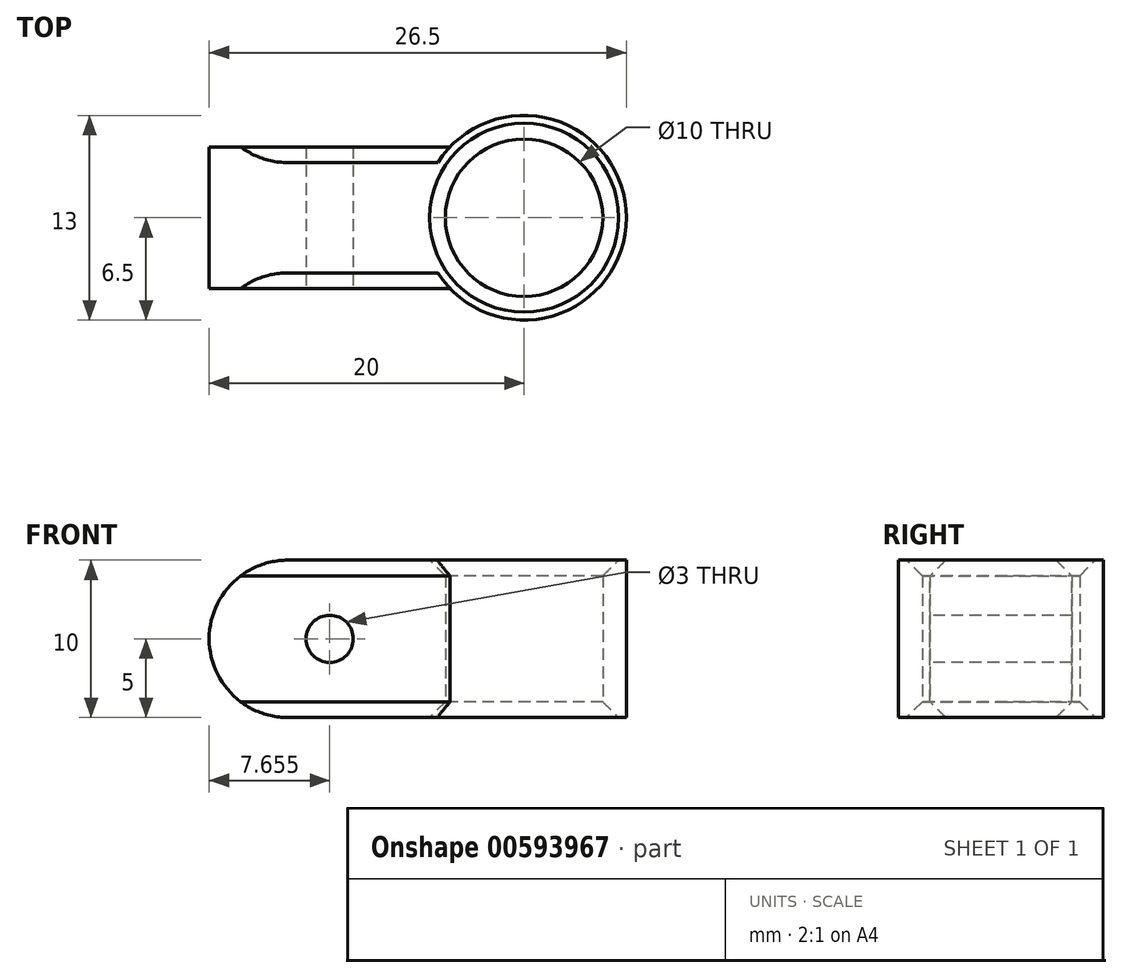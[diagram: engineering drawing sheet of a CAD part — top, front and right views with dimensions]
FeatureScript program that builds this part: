
annotation { "Feature Type Name" : "Feature", "Feature Type Description" : "" }
export const myFeature = defineFeature(function(context is Context, id is Id, definition is map)
    precondition{}
    {
        {
            var Q0;
            Q0=qCreatedBy(makeId("Top.planeOp"),FACE);
            var sketch = newSketch(context, id + "F0", { "sketchPlane" : qUnion([Q0])});
            skLineSegment(sketch, "E0.bottom", {"start": v(-10, 4.5) * mm, "end": v(10, 4.5) * mm});
            skLineSegment(sketch, "E0.top", {"start": v(-10, -4.5) * mm, "end": v(10, -4.5) * mm});
            skLineSegment(sketch, "E0.left", {"start": v(-10, 4.5) * mm, "end": v(-10, -4.5) * mm});
            skLineSegment(sketch, "E0.right", {"start": v(10, 4.5) * mm, "end": v(10, -4.5) * mm});
            skPoint(sketch, "E0.middle", {"position": v(0, 0) * mm});
            skCircle(sketch, "E1", {"center": v(10, 0) * mm, "radius": 5 * mm});
            skCircle(sketch, "E2", {"center": v(10, 0) * mm, "radius": 6.5 * mm});
            skSolve(sketch);
        }
        {
            var Q0;
            {var subQ0=sQuery(id+"F0.wireOp",EDGE,"E0.left");Q0=makeQuery(id+"F0.imprint","IMPRINT",FACE,{"disambiguationData":[TD([[makeQuery(id+"F0.imprint","IMPRINT",EDGE,{"derivedFrom":subQ0}),1.0]])]});}
            var Q1;
            {var subQ0=sQuery(id+"F0.wireOp",EDGE,"E2");var subQ1=sQuery(id+"F0.wireOp",EDGE,"E0.bottom");var subQ2=makeQuery(id+"F0.imprint","INTERSECT",VERTEX,{"derivedFrom":[subQ1,subQ0]});Q1=makeQuery(id+"F0.imprint","IMPRINT",FACE,{"disambiguationData":[TD([[makeQuery(id+"F0.imprint","IMPRINT",EDGE,{"disambiguationData":[TD([[subQ2,-1.0]])],"derivedFrom":subQ1}),-1.0]])]});}
            var Q2;
            {var subQ0=sQuery(id+"F0.wireOp",EDGE,"E2");var subQ1=sQuery(id+"F0.wireOp",EDGE,"E0.bottom");var subQ2=makeQuery(id+"F0.imprint","INTERSECT",VERTEX,{"derivedFrom":[subQ1,subQ0]});Q2=makeQuery(id+"F0.imprint","IMPRINT",FACE,{"disambiguationData":[TD([[makeQuery(id+"F0.imprint","IMPRINT",EDGE,{"disambiguationData":[TD([[subQ2,-1.0]])],"derivedFrom":subQ1}),1.0]])]});}
            extrude(context, id + "F1", {"entities" : qUnion([Q0, Q1, Q2]), "depth" : 10 * mm, "offsetDistance" : 25 * mm});
        }
        {
            var Q0;
            Q0=makeQuery(id+"F1.opExtrude","SWEPT_FACE",FACE,{"disambiguationData":[OSD([sQuery(id+"F0.wireOp",EDGE,"E0.top")])]});
            var sketch = newSketch(context, id + "F2", { "sketchPlane" : qUnion([Q0])});
            skLineSegment(sketch, "E3", {"start": v(-10, 10) * mm, "end": v(5.3, 0) * mm});
            skLineSegment(sketch, "E4", {"start": v(5.3, 10) * mm, "end": v(-10, 0) * mm});
            skPoint(sketch, "E5", {"position": v(-2.35, 5) * mm});
            skSolve(sketch);
        }
        {
            var Q0;
            Q0=sQuery(id+"F2.wireOp",VERTEX,"E5");
            var Q1;
            Q1=makeQuery(id+"F1.opExtrude","SWEPT_BODY",BODY,{"disambiguationData":[OSD([sQuery(id+"F0.wireOp",EDGE,"E0.bottom"),sQuery(id+"F0.wireOp",EDGE,"E0.top"),sQuery(id+"F0.wireOp",EDGE,"E0.left"),sQuery(id+"F0.wireOp",EDGE,"E1"),sQuery(id+"F0.wireOp",EDGE,"E2")])]});
            hole(context, id + "F3", {"style" : HoleStyle.SIMPLE, "endStyle" : HoleEndStyle.BLIND, "holeDiameter" : 3 * mm, "majorDiameter" : 5 * mm, "holeDepth" : 30 * mm, "isTappedThrough" : true, "tappedDepth" : 12 * mm, "tapClearance" : 3, "locations" : qUnion([Q0]), "scope" : qUnion([Q1])});
        }
        {
            var Q0;
            Q0=makeQuery(id+"F1.opExtrude","CAP_EDGE",EDGE,{"disambiguationData":[OSD([sQuery(id+"F0.wireOp",EDGE,"E1")])],"isStart":false});
            var Q1;
            Q1=makeQuery(id+"F1.opExtrude","CAP_EDGE",EDGE,{"disambiguationData":[OSD([sQuery(id+"F0.wireOp",EDGE,"E1")])],"isStart":true});
            var Q2;
            Q2=makeQuery(id+"F1.opExtrude","CAP_EDGE",EDGE,{"disambiguationData":[OSD([sQuery(id+"F0.wireOp",EDGE,"E0.bottom")])],"isStart":false});
            var Q3;
            Q3=makeQuery(id+"F1.opExtrude","CAP_EDGE",EDGE,{"disambiguationData":[OSD([sQuery(id+"F0.wireOp",EDGE,"E0.top")])],"isStart":false});
            var Q4;
            Q4=makeQuery(id+"F1.opExtrude","CAP_EDGE",EDGE,{"disambiguationData":[OSD([sQuery(id+"F0.wireOp",EDGE,"E0.top")])],"isStart":true});
            var Q5;
            Q5=makeQuery(id+"F1.opExtrude","CAP_EDGE",EDGE,{"disambiguationData":[OSD([sQuery(id+"F0.wireOp",EDGE,"E0.bottom")])],"isStart":true});
            chamfer(context, id + "F4", {"entities" : qUnion([Q0, Q1, Q2, Q3, Q4, Q5]), "width" : 1 * mm});
        }
        {
            var Q0;
            Q0=makeQuery(id+"F1.opExtrude","CAP_EDGE",EDGE,{"disambiguationData":[OSD([sQuery(id+"F0.wireOp",EDGE,"E0.left")])],"isStart":false});
            var Q1;
            Q1=makeQuery(id+"F1.opExtrude","CAP_EDGE",EDGE,{"disambiguationData":[OSD([sQuery(id+"F0.wireOp",EDGE,"E0.left")])],"isStart":true});
            fillet(context, id + "F5", {"entities" : qUnion([Q0, Q1]), "radius" : 5 * mm, "tangentPropagation" : true, "allowEdgeOverflow" : false});
        }
    });
